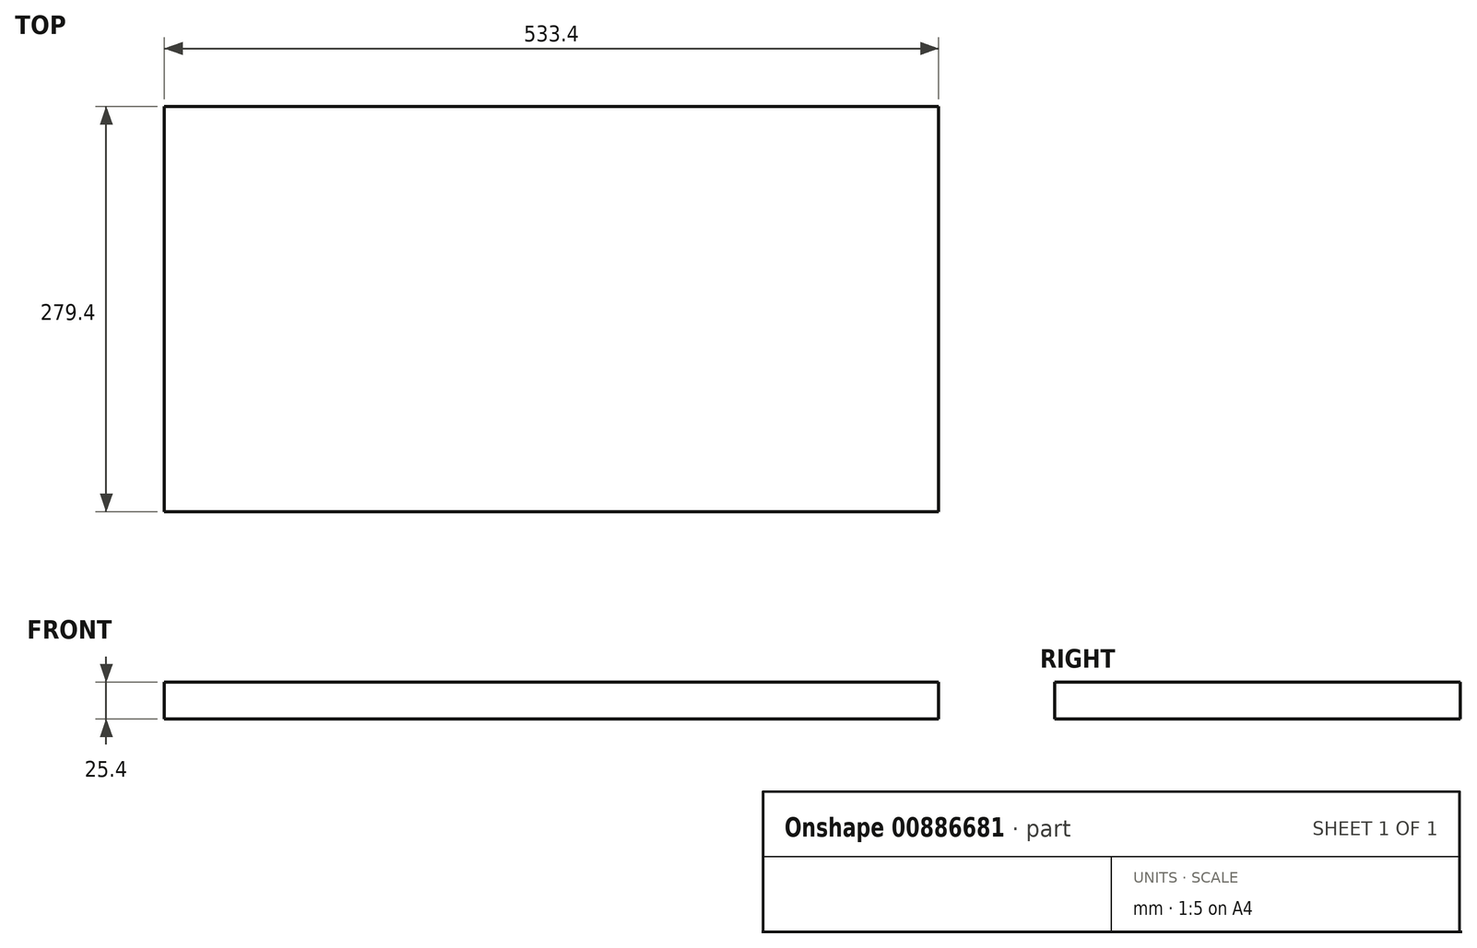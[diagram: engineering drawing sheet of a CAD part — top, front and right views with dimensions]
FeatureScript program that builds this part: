
annotation { "Feature Type Name" : "Feature", "Feature Type Description" : "" }
export const myFeature = defineFeature(function(context is Context, id is Id, definition is map)
    precondition{}
    {
        {
            var Q0;
            Q0=qCreatedBy(makeId("Top.planeOp"),FACE);
            var sketch = newSketch(context, id + "F0", { "sketchPlane" : qUnion([Q0])});
            skLineSegment(sketch, "E0.bottom", {"start": v(0, 0) * mm, "end": v(533.4, 0) * mm});
            skLineSegment(sketch, "E0.top", {"start": v(0, 279.4) * mm, "end": v(533.4, 279.4) * mm});
            skLineSegment(sketch, "E0.left", {"start": v(0, 0) * mm, "end": v(0, 279.4) * mm});
            skLineSegment(sketch, "E0.right", {"start": v(533.4, 0) * mm, "end": v(533.4, 279.4) * mm});
            skSolve(sketch);
        }
        {
            var Q0;
            Q0=makeQuery(id+"F0.imprint","IMPRINT",FACE,{"disambiguationData":[TD([[makeQuery(id+"F0.imprint","IMPRINT",EDGE,{"derivedFrom":sQuery(id+"F0.wireOp",EDGE,"E0.bottom")}),1.0]])]});
            extrude(context, id + "F1", {"entities" : qUnion([Q0]), "depth" : 25.4 * mm, "offsetDistance" : 25.4 * mm});
        }
    });
